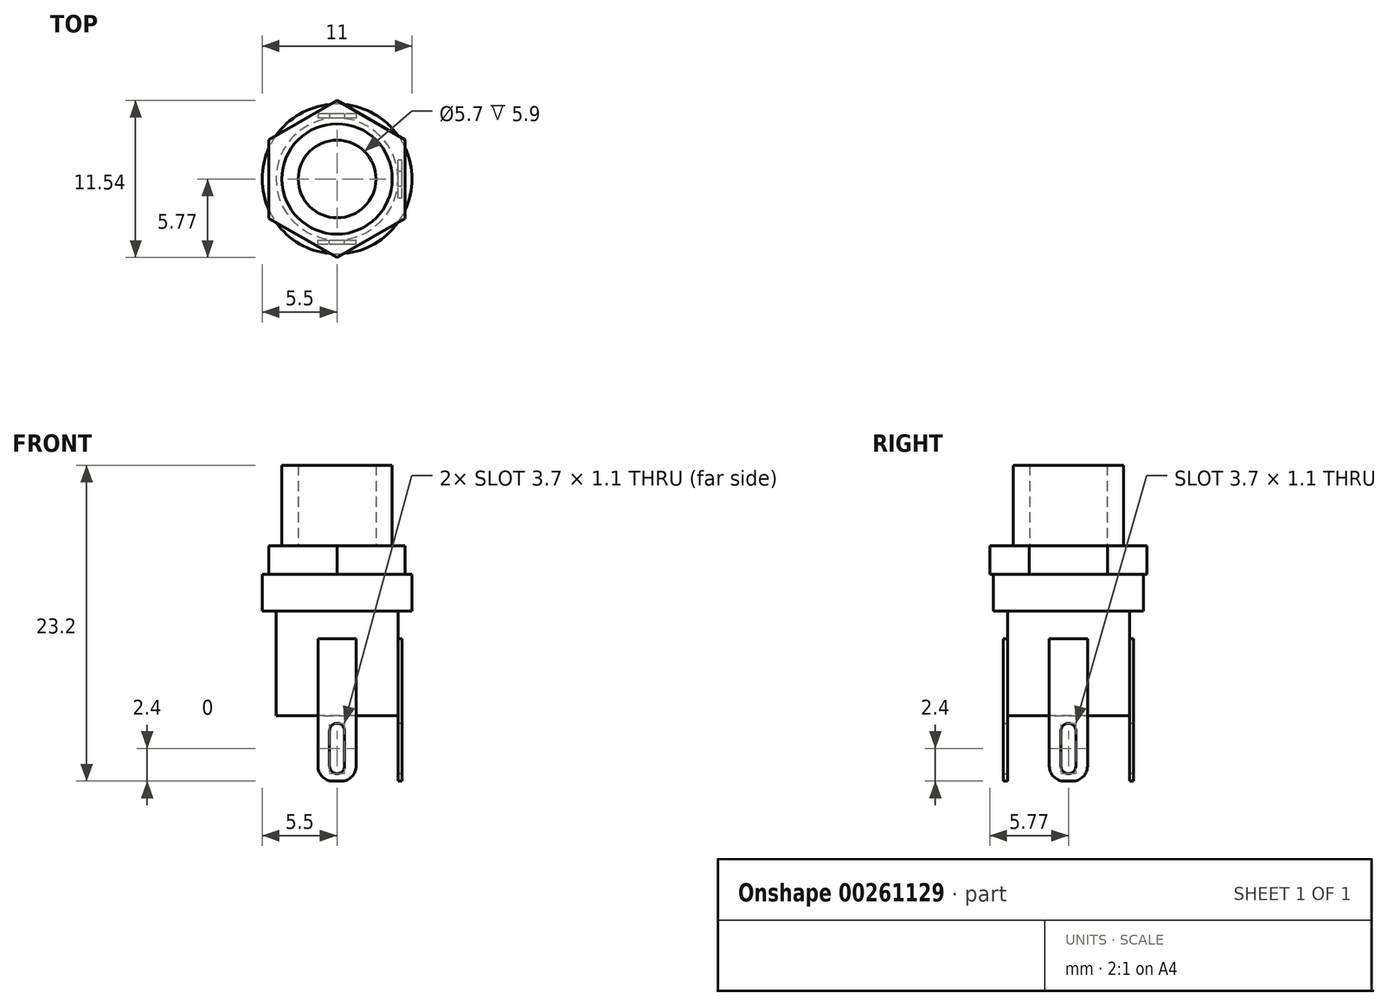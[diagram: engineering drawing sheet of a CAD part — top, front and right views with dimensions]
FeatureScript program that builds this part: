
annotation { "Feature Type Name" : "Feature", "Feature Type Description" : "" }
export const myFeature = defineFeature(function(context is Context, id is Id, definition is map)
    precondition{}
    {
        {
            var Q0;
            Q0=qCreatedBy(makeId("Top.planeOp"),FACE);
            var sketch = newSketch(context, id + "F0", { "sketchPlane" : qUnion([Q0])});
            skCircle(sketch, "E0", {"center": v(0, 0) * mm, "radius": 4.05 * mm});
            skCircle(sketch, "E1", {"center": v(0, 0) * mm, "radius": 2.85 * mm});
            skSolve(sketch);
        }
        {
            var Q0;
            Q0 = qSketchRegion(id + "F0", true);
            extrude(context, id + "F1", {"entities" : qUnion([Q0]), "depth" : 8 * mm});
        }
        {
            var Q0;
            Q0=makeQuery(id+"F1.opExtrude","CAP_FACE",FACE,{"disambiguationData":[OSD([sQuery(id+"F0.wireOp",EDGE,"E0"),sQuery(id+"F0.wireOp",EDGE,"E1")])],"isStart":true});
            var sketch = newSketch(context, id + "F2", { "sketchPlane" : qUnion([Q0])});
            skCircle(sketch, "E2.cCircle", {"center": v(0, 0) * mm, "radius": 5 * mm, "construction": true});
            skLineSegment(sketch, "E2.0", {"start": v(5, 2.89) * mm, "end": v(5, -2.89) * mm});
            skLineSegment(sketch, "E2.1", {"start": v(5, -2.89) * mm, "end": v(0, -5.77) * mm});
            skLineSegment(sketch, "E2.2", {"start": v(0, -5.77) * mm, "end": v(-5, -2.89) * mm});
            skLineSegment(sketch, "E2.3", {"start": v(-5, -2.89) * mm, "end": v(-5, 2.89) * mm});
            skLineSegment(sketch, "E2.4", {"start": v(-5, 2.89) * mm, "end": v(0, 5.77) * mm});
            skLineSegment(sketch, "E2.5", {"start": v(0, 5.77) * mm, "end": v(5, 2.89) * mm});
            skPoint(sketch, "E2.0.midPoint", {"position": v(5, 0) * mm});
            skSolve(sketch);
        }
        {
            var Q0;
            Q0 = qSketchRegion(id + "F2", true);
            extrude(context, id + "F3", {"entities" : qUnion([Q0]), "operationType" : NewBodyOperationType.ADD, "oppositeDirection" : true, "depth" : 2.1 * mm});
        }
        {
            var Q0;
            Q0=makeQuery(id+"F3.boolean.opBoolean","MERGE",FACE,{"derivedFrom":[makeQuery(id+"F1.opExtrude","CAP_FACE",FACE,{"disambiguationData":[OSD([sQuery(id+"F0.wireOp",EDGE,"E0"),sQuery(id+"F0.wireOp",EDGE,"E1")])],"isStart":true}),makeQuery(id+"F3.opExtrude","CAP_FACE",FACE,{"disambiguationData":[OSD([sQuery(id+"F2.wireOp",EDGE,"E2.0"),sQuery(id+"F2.wireOp",EDGE,"E2.1"),sQuery(id+"F2.wireOp",EDGE,"E2.2"),sQuery(id+"F2.wireOp",EDGE,"E2.3"),sQuery(id+"F2.wireOp",EDGE,"E2.4"),sQuery(id+"F2.wireOp",EDGE,"E2.5")])],"isStart":true})]});
            var sketch = newSketch(context, id + "F4", { "sketchPlane" : qUnion([Q0])});
            skCircle(sketch, "E3", {"center": v(0, 0) * mm, "radius": 5.5 * mm});
            skSolve(sketch);
        }
        {
            var Q0;
            Q0 = qSketchRegion(id + "F4", true);
            extrude(context, id + "F5", {"entities" : qUnion([Q0]), "operationType" : NewBodyOperationType.ADD, "depth" : 2.7 * mm});
        }
        {
            var Q0;
            Q0=makeQuery(id+"F5.opExtrude","CAP_FACE",FACE,{"disambiguationData":[OSD([sQuery(id+"F4.wireOp",EDGE,"E3")])],"isStart":false});
            var sketch = newSketch(context, id + "F6", { "sketchPlane" : qUnion([Q0])});
            skCircle(sketch, "E4", {"center": v(0, 0) * mm, "radius": 4.47 * mm});
            skSolve(sketch);
        }
        {
            var Q0;
            Q0=makeQuery(id+"F6.imprint","IMPRINT",FACE,{"disambiguationData":[TD([[makeQuery(id+"F6.imprint","IMPRINT",EDGE,{"derivedFrom":sQuery(id+"F6.wireOp",EDGE,"E4")}),1.0]])]});
            extrude(context, id + "F7", {"entities" : qUnion([Q0]), "operationType" : NewBodyOperationType.ADD, "depth" : 7.7 * mm});
        }
        {
            var Q0;
            Q0=qCreatedBy(makeId("Front.planeOp"),FACE);
            cPlane(context, id + "F8", {"entities" : qUnion([Q0]), "cplaneType" : CPlaneType.OFFSET, "offset" : 4.47 * mm, "width" : 150 * mm, "height" : 150 * mm});
        }
        {
            var Q0;
            Q0=qCreatedBy(id+"F8.planeOp",FACE);
            var sketch = newSketch(context, id + "F9", { "sketchPlane" : qUnion([Q0])});
            skLineSegment(sketch, "E5", {"start": v(-0.3, -15.2) * mm, "end": v(0.3, -15.2) * mm});
            skLineSegment(sketch, "E6", {"start": v(-1.4, -14.1) * mm, "end": v(-1.4, -4.74) * mm});
            skLineSegment(sketch, "E7", {"start": v(-1.4, 0) * mm, "end": v(1.4, 0) * mm});
            skLineSegment(sketch, "E8", {"start": v(1.4, -4.74) * mm, "end": v(1.4, -14.1) * mm});
            skLineSegment(sketch, "E9", {"start": v(-1.4, -4.74) * mm, "end": v(1.4, -4.74) * mm});
            skPoint(sketch, "E10.visualSharp", {"position": v(-1.4, -15.2) * mm});
            skArc(sketch, "E10.filletArc", {"start": v(-1.4, -14.1) * mm, "mid": v(-1.08, -14.88) * mm, "end": v(-0.3, -15.2) * mm});
            skPoint(sketch, "E11.visualSharp", {"position": v(1.4, -15.2) * mm});
            skArc(sketch, "E11.filletArc", {"start": v(0.3, -15.2) * mm, "mid": v(1.08, -14.88) * mm, "end": v(1.4, -14.1) * mm});
            skLineSegment(sketch, "E12", {"start": v(0, -14.1) * mm, "end": v(0, -11.5) * mm});
            skArc(sketch, "E13.0.startCap", {"start": v(0.55, -14.1) * mm, "mid": v(0, -14.65) * mm, "end": v(-0.55, -14.1) * mm});
            skArc(sketch, "E13.0.endCap", {"start": v(-0.55, -11.5) * mm, "mid": v(0, -10.95) * mm, "end": v(0.55, -11.5) * mm});
            skLineSegment(sketch, "E13.0.left", {"start": v(-0.55, -14.1) * mm, "end": v(-0.55, -11.5) * mm});
            skLineSegment(sketch, "E13.0.right", {"start": v(0.55, -14.1) * mm, "end": v(0.55, -11.5) * mm});
            skSolve(sketch);
        }
        {
            var Q0;
            Q0=makeQuery(id+"F9.imprint","IMPRINT",FACE,{"disambiguationData":[TD([[makeQuery(id+"F9.imprint","IMPRINT",EDGE,{"derivedFrom":sQuery(id+"F9.wireOp",EDGE,"E5")}),1.0]])]});
            extrude(context, id + "F10", {"entities" : qUnion([Q0]), "operationType" : NewBodyOperationType.ADD, "depth" : .3 * mm});
        }
        {
            var Q0;
            Q0=makeQuery(id+"F10.opExtrude","SWEPT_BODY",BODY,{"disambiguationData":[OSD([sQuery(id+"F9.wireOp",EDGE,"E5"),sQuery(id+"F9.wireOp",EDGE,"E6"),sQuery(id+"F9.wireOp",EDGE,"E8"),sQuery(id+"F9.wireOp",EDGE,"E9"),sQuery(id+"F9.wireOp",EDGE,"E10.filletArc"),sQuery(id+"F9.wireOp",EDGE,"E11.filletArc"),sQuery(id+"F9.wireOp",EDGE,"E13.0.startCap"),sQuery(id+"F9.wireOp",EDGE,"E13.0.endCap"),sQuery(id+"F9.wireOp",EDGE,"E13.0.left"),sQuery(id+"F9.wireOp",EDGE,"E13.0.right")])]});
            var Q1;
            Q1=makeQuery(id+"F1.opExtrude","CAP_EDGE",EDGE,{"disambiguationData":[OSD([sQuery(id+"F0.wireOp",EDGE,"E1")])],"isStart":false});
            circularPattern(context, id + "F11", {"entities" : qUnion([Q0]), "axis" : qUnion([Q1]), "angle" : 180 * degree, "instanceCount" : 3, "equalSpace" : true});
        }
    });
